# Revit family: 2919-070-001 -8-diverter
name_source: partatom
category: Plumbing Fixtures
revit_build: Autodesk Revit MEP 2016 (Build: 20150220_1215(x64)
units: mm (PartAtom-declared; Revit-internal decimal feet)

## family parameters
Cut with Voids When Loaded = No
Host = Face
OmniClass Number = 23.45.05.14
OmniClass Title = Plumbing Fixtures - Sanitary Washing Units
Part Type = Normal
Room Calculation Point = No
Round Connector Dimension = Use Diameter
Shared = Yes

## types (1)
- 2919-070-001 DIVERTER
    8- SV16 T/P Ligature Resistant Shower Diverter Valve = Yes
    Assembly Code = D2010710
    CW Connection = Yes
    CWFU = 0
    Default Elevation = 48"
    Description = SV16 Zenith Diverter Valve Assembly With Trim
    HW Connection = Yes
    HWFU = 0
    Manufacturer = Acorn Engineering Company
    Material = Stainless Steel-Acorn-Type 304-Satin
    Model = 2919-070-001
    Revised Date = 10/29/2019
    URL = http://www.acorneng.com
    Vent Connection = No
    WFU = 0
    Waste Connection = No

## geometry (parser evidence)
native form markers: Sweep x2
no freeform markers — native parametric forms only
